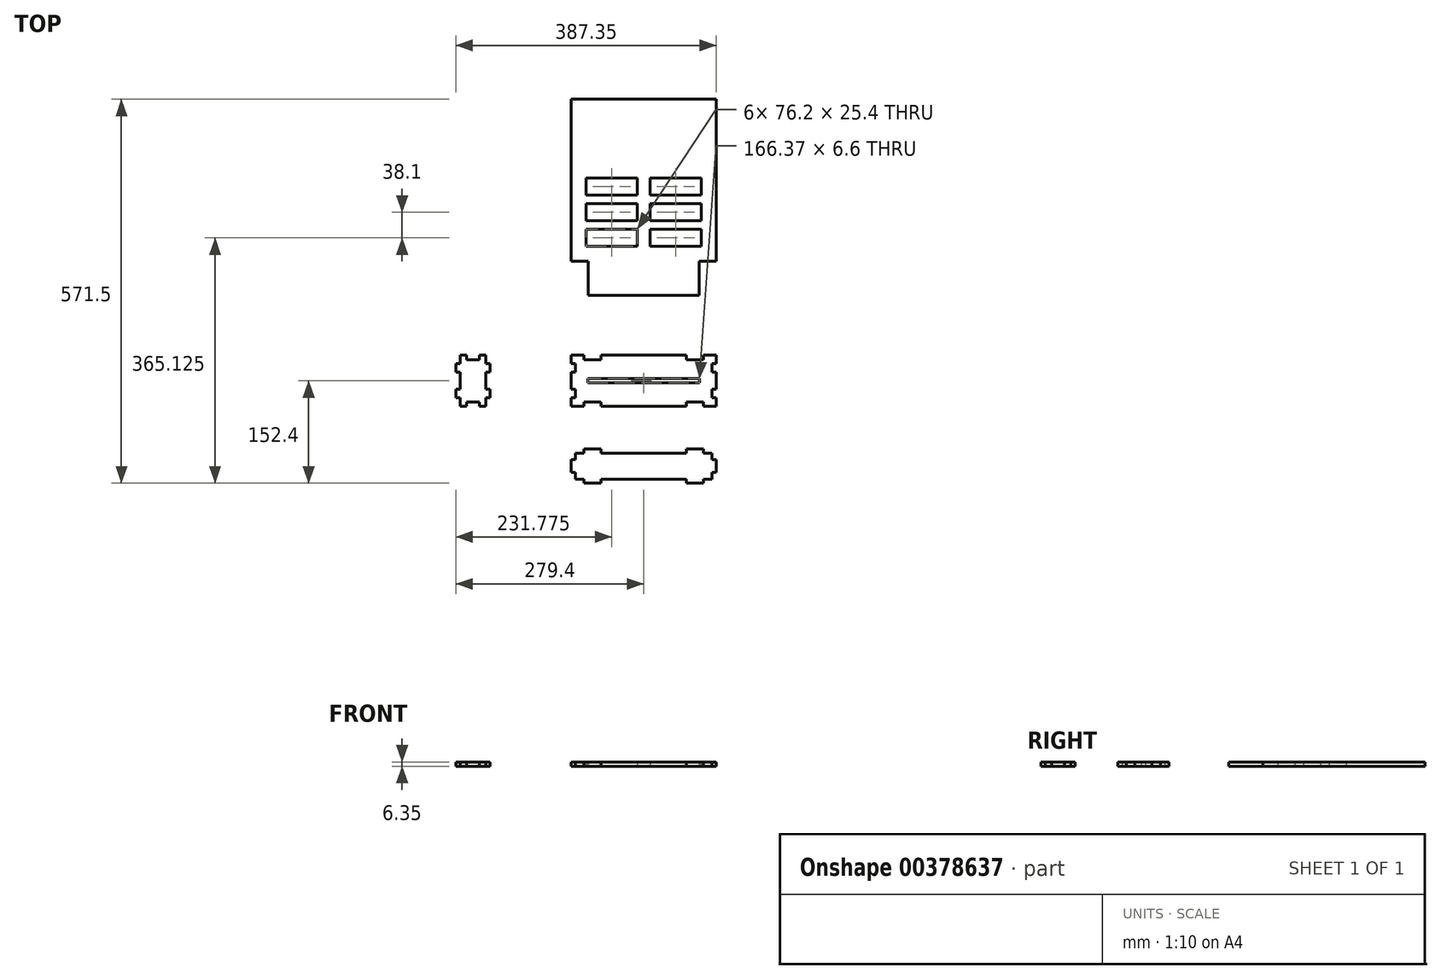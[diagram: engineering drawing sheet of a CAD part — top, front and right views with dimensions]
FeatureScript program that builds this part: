
annotation { "Feature Type Name" : "Feature", "Feature Type Description" : "" }
export const myFeature = defineFeature(function(context is Context, id is Id, definition is map)
    precondition{}
    {
        {
            var Q0;
            Q0=qCreatedBy(makeId("Top.planeOp"),FACE);
            var sketch = newSketch(context, id + "F0", { "sketchPlane" : qUnion([Q0])});
            skLineSegment(sketch, "E0.bottom", {"start": v(-107.95, 38.1) * mm, "end": v(107.95, 38.1) * mm});
            skLineSegment(sketch, "E0.top", {"start": v(-107.95, -38.1) * mm, "end": v(107.95, -38.1) * mm});
            skLineSegment(sketch, "E0.left", {"start": v(-107.95, 38.1) * mm, "end": v(-107.95, -38.1) * mm});
            skLineSegment(sketch, "E0.right", {"start": v(107.95, 38.1) * mm, "end": v(107.95, -38.1) * mm});
            skPoint(sketch, "E0.middle", {"position": v(0, 0) * mm});
            skLineSegment(sketch, "E1.bottom", {"start": v(-83.19, 3.3) * mm, "end": v(83.19, 3.3) * mm});
            skLineSegment(sketch, "E1.top", {"start": v(-83.19, -3.3) * mm, "end": v(83.19, -3.3) * mm});
            skLineSegment(sketch, "E1.left", {"start": v(-83.19, 3.3) * mm, "end": v(-83.19, -3.3) * mm});
            skLineSegment(sketch, "E1.right", {"start": v(83.19, 3.3) * mm, "end": v(83.19, -3.3) * mm});
            skLineSegment(sketch, "E2", {"start": v(-88.9, -38.1) * mm, "end": v(-88.9, -31.5) * mm});
            skLineSegment(sketch, "E3", {"start": v(-88.9, -31.5) * mm, "end": v(-63.5, -31.5) * mm});
            skLineSegment(sketch, "E4", {"start": v(-63.5, -31.5) * mm, "end": v(-63.5, -38.1) * mm});
            skLineSegment(sketch, "E5", {"start": v(63.5, -38.1) * mm, "end": v(63.5, -31.5) * mm});
            skLineSegment(sketch, "E6", {"start": v(63.5, -31.5) * mm, "end": v(88.9, -31.5) * mm});
            skLineSegment(sketch, "E7", {"start": v(88.9, -31.5) * mm, "end": v(88.9, -38.1) * mm});
            skLineSegment(sketch, "E8", {"start": v(-88.9, 38.1) * mm, "end": v(-88.9, 31.5) * mm});
            skLineSegment(sketch, "E9", {"start": v(-88.9, 31.5) * mm, "end": v(-63.5, 31.5) * mm});
            skLineSegment(sketch, "E10", {"start": v(-63.5, 31.5) * mm, "end": v(-63.5, 38.1) * mm});
            skLineSegment(sketch, "E11", {"start": v(63.5, 38.1) * mm, "end": v(63.5, 31.5) * mm});
            skLineSegment(sketch, "E12", {"start": v(63.5, 31.5) * mm, "end": v(88.9, 31.5) * mm});
            skLineSegment(sketch, "E13", {"start": v(88.9, 31.5) * mm, "end": v(88.9, 38.1) * mm});
            skLineSegment(sketch, "E14", {"start": v(-107.95, 25.4) * mm, "end": v(-101.35, 25.4) * mm});
            skLineSegment(sketch, "E15", {"start": v(-101.35, 25.4) * mm, "end": v(-101.35, 12.7) * mm});
            skLineSegment(sketch, "E16", {"start": v(-101.35, 12.7) * mm, "end": v(-107.95, 12.7) * mm});
            skLineSegment(sketch, "E17", {"start": v(-107.95, -12.7) * mm, "end": v(-101.35, -12.7) * mm});
            skLineSegment(sketch, "E18", {"start": v(-101.35, -12.7) * mm, "end": v(-101.35, -25.4) * mm});
            skLineSegment(sketch, "E19", {"start": v(-101.35, -25.4) * mm, "end": v(-107.95, -25.4) * mm});
            skLineSegment(sketch, "E20", {"start": v(107.95, 25.4) * mm, "end": v(101.35, 25.4) * mm});
            skLineSegment(sketch, "E21", {"start": v(101.35, 25.4) * mm, "end": v(101.35, 12.7) * mm});
            skLineSegment(sketch, "E22", {"start": v(101.35, 12.7) * mm, "end": v(107.95, 12.7) * mm});
            skLineSegment(sketch, "E23", {"start": v(107.95, -12.7) * mm, "end": v(101.35, -12.7) * mm});
            skLineSegment(sketch, "E24", {"start": v(101.35, -12.7) * mm, "end": v(101.35, -25.4) * mm});
            skLineSegment(sketch, "E25", {"start": v(101.35, -25.4) * mm, "end": v(107.95, -25.4) * mm});
            skPoint(sketch, "E26", {"position": v(-76.2, 31.5) * mm});
            skPoint(sketch, "E27", {"position": v(76.2, 31.5) * mm});
            skPoint(sketch, "E28", {"position": v(76.2, -31.5) * mm});
            skPoint(sketch, "E29", {"position": v(-76.2, -31.5) * mm});
            skLineSegment(sketch, "E30.bottom", {"start": v(-273.3, 38.1) * mm, "end": v(-234.7, 38.1) * mm});
            skLineSegment(sketch, "E30.top", {"start": v(-273.3, -38.1) * mm, "end": v(-234.7, -38.1) * mm});
            skLineSegment(sketch, "E30.left", {"start": v(-273.3, 38.1) * mm, "end": v(-273.3, -38.1) * mm});
            skLineSegment(sketch, "E30.right", {"start": v(-234.7, 38.1) * mm, "end": v(-234.7, -38.1) * mm});
            skLineSegment(sketch, "E31", {"start": v(-234.7, 25.27) * mm, "end": v(-228.6, 25.27) * mm});
            skLineSegment(sketch, "E32", {"start": v(-228.6, 25.27) * mm, "end": v(-228.6, 12.83) * mm});
            skLineSegment(sketch, "E33", {"start": v(-228.6, 12.83) * mm, "end": v(-234.7, 12.83) * mm});
            skLineSegment(sketch, "E34", {"start": v(-273.3, 12.83) * mm, "end": v(-279.4, 12.83) * mm});
            skLineSegment(sketch, "E35", {"start": v(-279.4, 12.83) * mm, "end": v(-279.4, 25.27) * mm});
            skLineSegment(sketch, "E36", {"start": v(-279.4, 25.27) * mm, "end": v(-273.3, 25.27) * mm});
            skLineSegment(sketch, "E37", {"start": v(-273.3, -12.83) * mm, "end": v(-279.4, -12.83) * mm});
            skLineSegment(sketch, "E38", {"start": v(-279.4, -12.83) * mm, "end": v(-279.4, -25.27) * mm});
            skLineSegment(sketch, "E39", {"start": v(-279.4, -25.27) * mm, "end": v(-273.3, -25.27) * mm});
            skLineSegment(sketch, "E40", {"start": v(-234.7, -25.27) * mm, "end": v(-228.6, -25.27) * mm});
            skLineSegment(sketch, "E41", {"start": v(-228.6, -25.27) * mm, "end": v(-228.6, -12.83) * mm});
            skLineSegment(sketch, "E42", {"start": v(-228.6, -12.83) * mm, "end": v(-234.7, -12.83) * mm});
            skPoint(sketch, "E43", {"position": v(-228.6, 19.05) * mm});
            skPoint(sketch, "E44", {"position": v(-228.6, -19.05) * mm});
            skPoint(sketch, "E45", {"position": v(-279.4, -19.05) * mm});
            skPoint(sketch, "E46", {"position": v(-279.4, 19.05) * mm});
            skPoint(sketch, "E47", {"position": v(-101.35, 19.05) * mm});
            skPoint(sketch, "E48", {"position": v(-101.35, -19.05) * mm});
            skPoint(sketch, "E49", {"position": v(-254, 38.1) * mm});
            skLineSegment(sketch, "E50.bottom", {"start": v(-107.95, -107.7) * mm, "end": v(107.95, -107.7) * mm});
            skLineSegment(sketch, "E50.top", {"start": v(-107.95, -146.3) * mm, "end": v(107.95, -146.3) * mm});
            skLineSegment(sketch, "E50.left", {"start": v(-107.95, -107.7) * mm, "end": v(-107.95, -146.3) * mm});
            skLineSegment(sketch, "E50.right", {"start": v(107.95, -107.7) * mm, "end": v(107.95, -146.3) * mm});
            skLineSegment(sketch, "E51", {"start": v(-88.77, -107.7) * mm, "end": v(-88.77, -101.6) * mm});
            skLineSegment(sketch, "E52", {"start": v(-88.77, -101.6) * mm, "end": v(-63.63, -101.6) * mm});
            skLineSegment(sketch, "E53", {"start": v(-63.63, -101.6) * mm, "end": v(-63.63, -107.7) * mm});
            skLineSegment(sketch, "E54", {"start": v(-88.77, -146.3) * mm, "end": v(-88.77, -152.4) * mm});
            skLineSegment(sketch, "E55", {"start": v(-88.77, -152.4) * mm, "end": v(-63.63, -152.4) * mm});
            skLineSegment(sketch, "E56", {"start": v(-63.63, -152.4) * mm, "end": v(-63.63, -146.3) * mm});
            skLineSegment(sketch, "E57", {"start": v(63.63, -107.7) * mm, "end": v(63.63, -101.6) * mm});
            skLineSegment(sketch, "E58", {"start": v(63.63, -101.6) * mm, "end": v(88.77, -101.6) * mm});
            skLineSegment(sketch, "E59", {"start": v(88.77, -101.6) * mm, "end": v(88.77, -107.7) * mm});
            skLineSegment(sketch, "E60", {"start": v(63.63, -146.3) * mm, "end": v(63.63, -152.4) * mm});
            skLineSegment(sketch, "E61", {"start": v(63.63, -152.4) * mm, "end": v(88.77, -152.4) * mm});
            skLineSegment(sketch, "E62", {"start": v(88.77, -152.4) * mm, "end": v(88.77, -146.3) * mm});
            skPoint(sketch, "E63", {"position": v(-76.2, -101.6) * mm});
            skPoint(sketch, "E64", {"position": v(76.2, -101.6) * mm});
            skPoint(sketch, "E65", {"position": v(76.2, -152.4) * mm});
            skPoint(sketch, "E66", {"position": v(-76.2, -152.4) * mm});
            skPoint(sketch, "E67", {"position": v(107.95, -127) * mm});
            skLineSegment(sketch, "E68", {"start": v(-273.3, 31.5) * mm, "end": v(-263.4, 31.5) * mm});
            skLineSegment(sketch, "E69", {"start": v(-273.3, -31.5) * mm, "end": v(-263.4, -31.5) * mm});
            skLineSegment(sketch, "E70", {"start": v(-107.95, -117.48) * mm, "end": v(-101.85, -117.48) * mm});
            skLineSegment(sketch, "E71", {"start": v(-101.85, -117.48) * mm, "end": v(-101.85, -107.7) * mm});
            skLineSegment(sketch, "E72", {"start": v(-107.95, -136.53) * mm, "end": v(-101.85, -136.53) * mm});
            skLineSegment(sketch, "E73", {"start": v(-101.85, -136.53) * mm, "end": v(-101.85, -146.3) * mm});
            skLineSegment(sketch, "E74", {"start": v(101.85, -107.7) * mm, "end": v(101.85, -117.48) * mm});
            skLineSegment(sketch, "E75", {"start": v(101.85, -117.48) * mm, "end": v(107.95, -117.48) * mm});
            skLineSegment(sketch, "E76", {"start": v(101.85, -146.3) * mm, "end": v(101.85, -136.53) * mm});
            skLineSegment(sketch, "E77", {"start": v(101.85, -136.53) * mm, "end": v(107.95, -136.53) * mm});
            skLineSegment(sketch, "E78", {"start": v(-263.4, 38.1) * mm, "end": v(-263.4, 31.5) * mm});
            skLineSegment(sketch, "E79", {"start": v(-244.6, 38.1) * mm, "end": v(-244.6, 31.5) * mm});
            skLineSegment(sketch, "E80", {"start": v(-263.4, -31.5) * mm, "end": v(-263.4, -38.1) * mm});
            skLineSegment(sketch, "E81", {"start": v(-244.6, -31.5) * mm, "end": v(-244.6, -38.1) * mm});
            skLineSegment(sketch, "E82.trimOffspring", {"start": v(-244.6, 31.5) * mm, "end": v(-234.7, 31.5) * mm});
            skLineSegment(sketch, "E83.trimOffspring", {"start": v(-244.6, -31.5) * mm, "end": v(-234.7, -31.5) * mm});
            skLineSegment(sketch, "E84", {"start": v(-263.4, 31.5) * mm, "end": v(-244.6, 31.5) * mm});
            skPoint(sketch, "E85", {"position": v(-254, 31.5) * mm});
            skLineSegment(sketch, "E86", {"start": v(-263.4, -31.5) * mm, "end": v(-244.6, -31.5) * mm});
            skPoint(sketch, "E87", {"position": v(-254, -31.5) * mm});
            skLineSegment(sketch, "E88.bottom", {"start": v(-107.95, 419.1) * mm, "end": v(107.95, 419.1) * mm});
            skLineSegment(sketch, "E88.top", {"start": v(-107.95, 177.8) * mm, "end": v(107.95, 177.8) * mm});
            skLineSegment(sketch, "E88.left", {"start": v(-107.95, 419.1) * mm, "end": v(-107.95, 177.8) * mm});
            skLineSegment(sketch, "E88.right", {"start": v(107.95, 419.1) * mm, "end": v(107.95, 177.8) * mm});
            skLineSegment(sketch, "E89", {"start": v(-82.55, 177.8) * mm, "end": v(-82.55, 127) * mm});
            skLineSegment(sketch, "E90", {"start": v(-82.55, 127) * mm, "end": v(82.55, 127) * mm});
            skLineSegment(sketch, "E91", {"start": v(82.55, 127) * mm, "end": v(82.55, 177.8) * mm});
            skPoint(sketch, "E92", {"position": v(0, 177.8) * mm});
            skPoint(sketch, "E93", {"position": v(0, 127) * mm});
            skLineSegment(sketch, "E94.bottom", {"start": v(-85.72, 301.62) * mm, "end": v(-9.53, 301.62) * mm});
            skLineSegment(sketch, "E94.top", {"start": v(-85.72, 276.23) * mm, "end": v(-9.53, 276.23) * mm});
            skLineSegment(sketch, "E94.left", {"start": v(-85.73, 301.62) * mm, "end": v(-85.72, 276.22) * mm});
            skLineSegment(sketch, "E94.right", {"start": v(-9.52, 301.63) * mm, "end": v(-9.52, 276.22) * mm});
            skLineSegment(sketch, "E95.bottom", {"start": v(9.53, 301.63) * mm, "end": v(85.72, 301.63) * mm});
            skLineSegment(sketch, "E95.top", {"start": v(9.52, 276.22) * mm, "end": v(85.73, 276.22) * mm});
            skLineSegment(sketch, "E95.left", {"start": v(9.53, 301.63) * mm, "end": v(9.53, 276.22) * mm});
            skLineSegment(sketch, "E95.right", {"start": v(85.73, 301.63) * mm, "end": v(85.73, 276.22) * mm});
            skLineSegment(sketch, "E96.bottom", {"start": v(-85.72, 263.52) * mm, "end": v(-9.53, 263.52) * mm});
            skLineSegment(sketch, "E96.top", {"start": v(-85.72, 238.12) * mm, "end": v(-9.53, 238.12) * mm});
            skLineSegment(sketch, "E96.left", {"start": v(-85.72, 263.52) * mm, "end": v(-85.72, 238.12) * mm});
            skLineSegment(sketch, "E96.right", {"start": v(-9.53, 263.52) * mm, "end": v(-9.53, 238.12) * mm});
            skLineSegment(sketch, "E97.bottom", {"start": v(9.53, 263.52) * mm, "end": v(85.72, 263.52) * mm});
            skLineSegment(sketch, "E97.top", {"start": v(9.52, 238.12) * mm, "end": v(85.72, 238.12) * mm});
            skLineSegment(sketch, "E97.left", {"start": v(9.53, 263.52) * mm, "end": v(9.53, 238.12) * mm});
            skLineSegment(sketch, "E97.right", {"start": v(85.73, 263.52) * mm, "end": v(85.73, 238.12) * mm});
            skLineSegment(sketch, "E98.bottom", {"start": v(-85.72, 225.42) * mm, "end": v(-9.53, 225.42) * mm});
            skLineSegment(sketch, "E98.top", {"start": v(-85.72, 200.03) * mm, "end": v(-9.53, 200.03) * mm});
            skLineSegment(sketch, "E98.left", {"start": v(-85.72, 225.42) * mm, "end": v(-85.72, 200.03) * mm});
            skLineSegment(sketch, "E98.right", {"start": v(-9.53, 225.42) * mm, "end": v(-9.53, 200.03) * mm});
            skLineSegment(sketch, "E99.bottom", {"start": v(9.52, 225.42) * mm, "end": v(85.73, 225.42) * mm});
            skLineSegment(sketch, "E99.top", {"start": v(9.52, 200.03) * mm, "end": v(85.72, 200.03) * mm});
            skLineSegment(sketch, "E99.left", {"start": v(9.52, 225.42) * mm, "end": v(9.52, 200.03) * mm});
            skLineSegment(sketch, "E99.right", {"start": v(85.73, 225.42) * mm, "end": v(85.73, 200.03) * mm});
            skPoint(sketch, "E100", {"position": v(-47.63, 301.63) * mm});
            skPoint(sketch, "E101", {"position": v(-47.63, 263.52) * mm});
            skPoint(sketch, "E102", {"position": v(-47.62, 225.42) * mm});
            skPoint(sketch, "E103", {"position": v(-47.62, 225.43) * mm});
            skPoint(sketch, "E104", {"position": v(47.62, 225.43) * mm});
            skPoint(sketch, "E105", {"position": v(47.63, 225.42) * mm});
            skPoint(sketch, "E106", {"position": v(47.63, 263.52) * mm});
            skPoint(sketch, "E107", {"position": v(47.63, 301.63) * mm});
            skLineSegment(sketch, "E108", {"start": v(-85.73, 276.22) * mm, "end": v(-85.72, 263.52) * mm});
            skLineSegment(sketch, "E109", {"start": v(-85.72, 238.12) * mm, "end": v(-85.72, 225.42) * mm});
            skLineSegment(sketch, "E110", {"start": v(-9.53, 301.63) * mm, "end": v(9.53, 301.63) * mm});
            skPoint(sketch, "E111", {"position": v(0, 301.63) * mm});
            skSolve(sketch);
        }
        {
            var Q0;
            Q0=makeQuery(id+"F0.imprint","IMPRINT",FACE,{"disambiguationData":[TD([[makeQuery(id+"F0.imprint","IMPRINT",EDGE,{"derivedFrom":sQuery(id+"F0.wireOp",EDGE,"E0.bottom")}),-1.0]])]});
            extrude(context, id + "F1", {"entities" : qUnion([Q0]), "depth" : 6.35 * mm});
        }
        {
            var Q0;
            {var subQ0=sQuery(id+"F0.wireOp",EDGE,"E51");Q0=makeQuery(id+"F0.imprint","IMPRINT",FACE,{"disambiguationData":[TD([[makeQuery(id+"F0.imprint","IMPRINT",EDGE,{"derivedFrom":subQ0}),-1.0]])]});}
            var Q1;
            {var subQ0=sQuery(id+"F0.wireOp",EDGE,"E54");Q1=makeQuery(id+"F0.imprint","IMPRINT",FACE,{"disambiguationData":[TD([[makeQuery(id+"F0.imprint","IMPRINT",EDGE,{"derivedFrom":subQ0}),1.0]])]});}
            var Q2;
            {var subQ0=sQuery(id+"F0.wireOp",EDGE,"E60");Q2=makeQuery(id+"F0.imprint","IMPRINT",FACE,{"disambiguationData":[TD([[makeQuery(id+"F0.imprint","IMPRINT",EDGE,{"derivedFrom":subQ0}),1.0]])]});}
            var Q3;
            {var subQ0=sQuery(id+"F0.wireOp",EDGE,"E57");Q3=makeQuery(id+"F0.imprint","IMPRINT",FACE,{"disambiguationData":[TD([[makeQuery(id+"F0.imprint","IMPRINT",EDGE,{"derivedFrom":subQ0}),-1.0]])]});}
            var Q4;
            {var subQ3=sQuery(id+"F0.wireOp",EDGE,"E70");Q4=makeQuery(id+"F0.imprint","IMPRINT",FACE,{"disambiguationData":[TD([[makeQuery(id+"F0.imprint","IMPRINT",EDGE,{"derivedFrom":subQ3}),-1.0]])]});}
            extrude(context, id + "F2", {"entities" : qUnion([Q0, Q1, Q2, Q3, Q4]), "depth" : 6.35 * mm});
        }
        {
            var Q0;
            {var subQ0=sQuery(id+"F0.wireOp",EDGE,"E31");Q0=makeQuery(id+"F0.imprint","IMPRINT",FACE,{"disambiguationData":[TD([[makeQuery(id+"F0.imprint","IMPRINT",EDGE,{"derivedFrom":subQ0}),-1.0]])]});}
            var Q1;
            {var subQ0=sQuery(id+"F0.wireOp",EDGE,"E40");Q1=makeQuery(id+"F0.imprint","IMPRINT",FACE,{"disambiguationData":[TD([[makeQuery(id+"F0.imprint","IMPRINT",EDGE,{"derivedFrom":subQ0}),1.0]])]});}
            var Q2;
            {var subQ0=sQuery(id+"F0.wireOp",EDGE,"E37");Q2=makeQuery(id+"F0.imprint","IMPRINT",FACE,{"disambiguationData":[TD([[makeQuery(id+"F0.imprint","IMPRINT",EDGE,{"derivedFrom":subQ0}),1.0]])]});}
            var Q3;
            {var subQ0=sQuery(id+"F0.wireOp",EDGE,"E34");Q3=makeQuery(id+"F0.imprint","IMPRINT",FACE,{"disambiguationData":[TD([[makeQuery(id+"F0.imprint","IMPRINT",EDGE,{"derivedFrom":subQ0}),-1.0]])]});}
            var Q4;
            {var subQ5=sQuery(id+"F0.wireOp",EDGE,"E68");Q4=makeQuery(id+"F0.imprint","IMPRINT",FACE,{"disambiguationData":[TD([[makeQuery(id+"F0.imprint","IMPRINT",EDGE,{"derivedFrom":subQ5}),-1.0]])]});}
            var Q5;
            {var subQ3=sQuery(id+"F0.wireOp",EDGE,"E79");Q5=makeQuery(id+"F0.imprint","IMPRINT",FACE,{"disambiguationData":[TD([[makeQuery(id+"F0.imprint","IMPRINT",EDGE,{"derivedFrom":subQ3}),1.0]])]});}
            var Q6;
            {var subQ4=sQuery(id+"F0.wireOp",EDGE,"E68");Q6=makeQuery(id+"F0.imprint","IMPRINT",FACE,{"disambiguationData":[TD([[makeQuery(id+"F0.imprint","IMPRINT",EDGE,{"derivedFrom":subQ4}),1.0]])]});}
            var Q7;
            {var subQ4=sQuery(id+"F0.wireOp",EDGE,"E69");Q7=makeQuery(id+"F0.imprint","IMPRINT",FACE,{"disambiguationData":[TD([[makeQuery(id+"F0.imprint","IMPRINT",EDGE,{"derivedFrom":subQ4}),-1.0]])]});}
            var Q8;
            {var subQ3=sQuery(id+"F0.wireOp",EDGE,"E81");Q8=makeQuery(id+"F0.imprint","IMPRINT",FACE,{"disambiguationData":[TD([[makeQuery(id+"F0.imprint","IMPRINT",EDGE,{"derivedFrom":subQ3}),1.0]])]});}
            extrude(context, id + "F3", {"entities" : qUnion([Q0, Q1, Q2, Q3, Q4, Q5, Q6, Q7, Q8]), "depth" : 6.35 * mm});
        }
        {
            var Q0;
            Q0=makeQuery(id+"F0.imprint","IMPRINT",FACE,{"disambiguationData":[TD([[makeQuery(id+"F0.imprint","IMPRINT",EDGE,{"derivedFrom":sQuery(id+"F0.wireOp",EDGE,"E88.bottom")}),-1.0]])]});
            var Q1;
            {var subQ0=sQuery(id+"F0.wireOp",EDGE,"E89");Q1=makeQuery(id+"F0.imprint","IMPRINT",FACE,{"disambiguationData":[TD([[makeQuery(id+"F0.imprint","IMPRINT",EDGE,{"derivedFrom":subQ0}),1.0]])]});}
            extrude(context, id + "F4", {"entities" : qUnion([Q0, Q1]), "depth" : 6.35 * mm});
        }
    });
